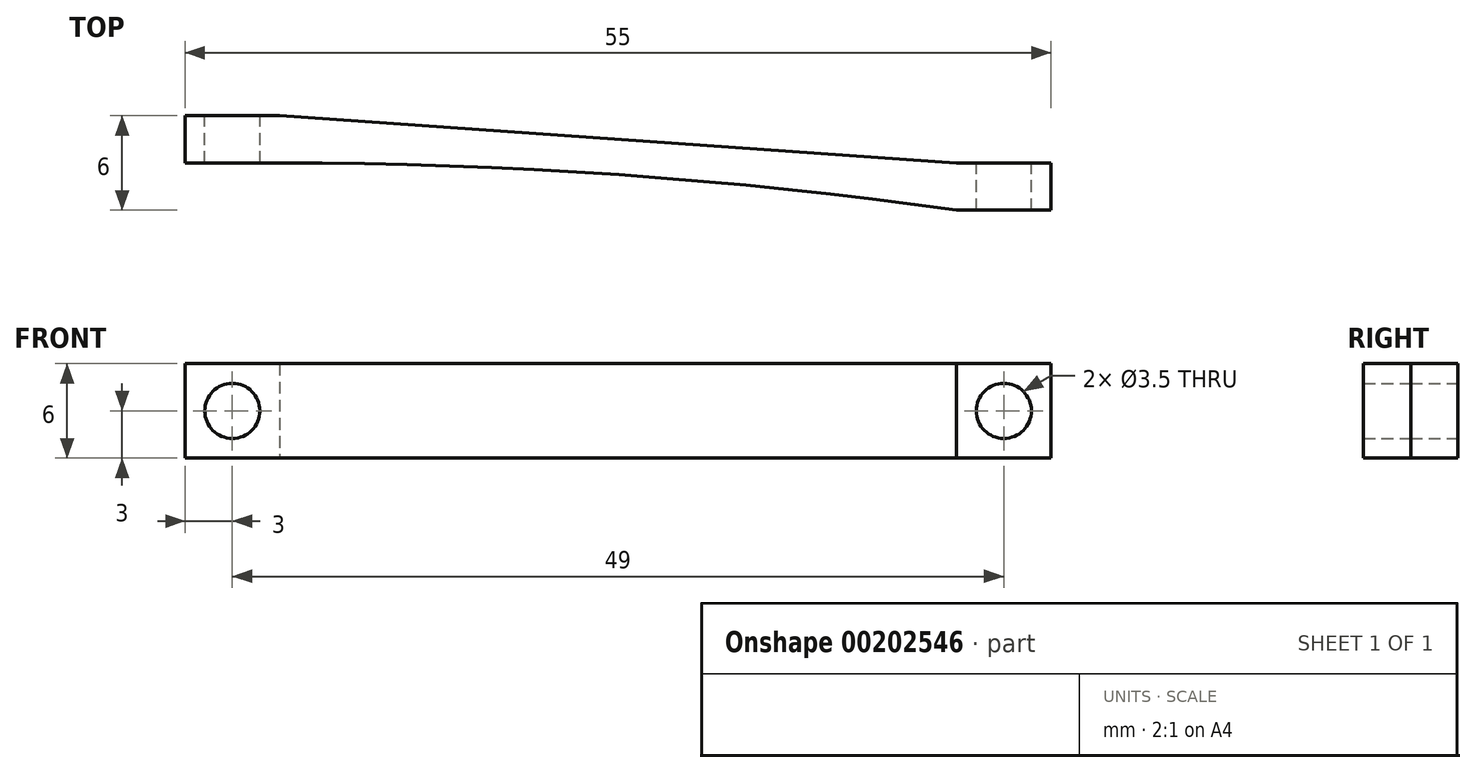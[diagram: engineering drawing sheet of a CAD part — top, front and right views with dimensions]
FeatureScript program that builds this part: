
annotation { "Feature Type Name" : "Feature", "Feature Type Description" : "" }
export const myFeature = defineFeature(function(context is Context, id is Id, definition is map)
    precondition{}
    {
        {
            var Q0;
            Q0=qCreatedBy(makeId("Top.planeOp"),FACE);
            var sketch = newSketch(context, id + "F0", { "sketchPlane" : qUnion([Q0])});
            skArc(sketch, "E0", {"start": v(43, -3) * mm, "mid": v(21.55, -0.75) * mm, "end": v(0, 0) * mm});
            skLineSegment(sketch, "E1", {"start": v(0, 0) * mm, "end": v(43, 0) * mm, "construction": true});
            skLineSegment(sketch, "E2", {"start": v(0, 0) * mm, "end": v(0, -3) * mm, "construction": true});
            skLineSegment(sketch, "E3", {"start": v(0, -3) * mm, "end": v(43, -3) * mm, "construction": true});
            skLineSegment(sketch, "E4", {"start": v(43, -3) * mm, "end": v(43, 0) * mm, "construction": true});
            skLineSegment(sketch, "E5", {"start": v(43, -3) * mm, "end": v(49, -3) * mm});
            skLineSegment(sketch, "E6", {"start": v(0, 0) * mm, "end": v(-6, 0) * mm});
            skLineSegment(sketch, "E7.0", {"start": v(0, 3) * mm, "end": v(-6, 3) * mm});
            skLineSegment(sketch, "E8", {"start": v(-6, 0) * mm, "end": v(-6, 3) * mm});
            skLineSegment(sketch, "E9", {"start": v(49, -3) * mm, "end": v(49, 0) * mm});
            skLineSegment(sketch, "E10", {"start": v(0, 3) * mm, "end": v(43, 0) * mm});
            skLineSegment(sketch, "E11", {"start": v(0, 0) * mm, "end": v(0, 3) * mm, "construction": true});
            skLineSegment(sketch, "E12", {"start": v(43, 0) * mm, "end": v(49, 0) * mm});
            skSolve(sketch);
        }
        {
            var Q0;
            Q0 = qSketchRegion(id + "F0", true);
            extrude(context, id + "F1", {"entities" : qUnion([Q0]), "depth" : 6 * mm});
        }
        {
            var Q0;
            Q0=makeQuery(id+"F1.opExtrude","SWEPT_FACE",FACE,{"disambiguationData":[OSD([sQuery(id+"F0.wireOp",EDGE,"E7.0")])]});
            var sketch = newSketch(context, id + "F2", { "sketchPlane" : qUnion([Q0])});
            skLineSegment(sketch, "E13", {"start": v(6, 6) * mm, "end": v(0, 0) * mm, "construction": true});
            skCircle(sketch, "E14", {"center": v(3, 3) * mm, "radius": 1.75 * mm});
            skPoint(sketch, "E15.0", {"position": v(-49, 0) * mm});
            skLineSegment(sketch, "E16", {"start": v(-43, 6) * mm, "end": v(-49, 0) * mm, "construction": true});
            skCircle(sketch, "E17", {"center": v(-46, 3) * mm, "radius": 1.75 * mm});
            skPoint(sketch, "E18.0", {"position": v(-43, 6) * mm});
            skSolve(sketch);
        }
        {
            var Q0;
            Q0 = qSketchRegion(id + "F2", true);
            extrude(context, id + "F3", {"entities" : qUnion([Q0]), "operationType" : NewBodyOperationType.REMOVE, "endBound" : BoundingType.THROUGH_ALL, "oppositeDirection" : true, "depth" : 25 * mm});
        }
    });
